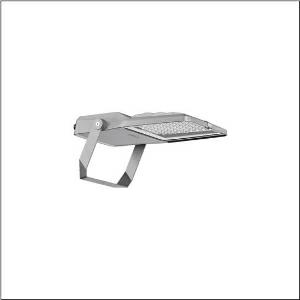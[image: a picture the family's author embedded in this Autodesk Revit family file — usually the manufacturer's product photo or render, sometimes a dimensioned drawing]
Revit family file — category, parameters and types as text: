
# Revit family: floodlight_fl_21_iq_mini___pl33t_5xa7771d2f1a_9c88
name_source: partatom
category: Lighting Fixtures
units: mm (PartAtom-declared; Revit-internal decimal feet)

## family parameters
Cut with Voids When Loaded = No
Host = Face
Light Source = No
Part Type = Normal
Room Calculation Point = No
Round Connector Dimension = Use Diameter
Shared = No

## types (1)
- --- (1 x LED, 17620 lm, 143 W, 3000K)
    Apparent Load = 143 VA
    CIE Flux Codes = 26 75 99 100 100
    Color Rendering = 70
    Color Temperature = 3000K
    Default Elevation = 1800 mm
    Description = Floodlight FL 21 iQ mini, floodlight, primary light control with lens, of PMMA, primary optical cover: protective disc, of toughened safety glass, transparent, light distribution: PL33T, light emission: direct distribution, installation type: surface-mounted, LED, High Power LED, rated luminous flux: 17.620lm, luminous efficacy: 123lm/W, light colour: 730, colour temperature: 3000K, control gear: iQ Comfort/DALI, control: Auto-Match, Temp-Guard, Lumen-Switch, Night-Set, Smart-Wire, Light-Fading, Desk-Remote (wireless, voltage-free reading and setting of iQ features in the workshop via application-optimized NFC function/RFID function), optimised constant luminous flux control (CLO 2.0), with terminal, 6-pole, mains connection: 220..240V, AC, 50/60Hz, start of lifetime: 143W, end of service life: 152W, reduction: 61W, luminaire housing, of diecast aluminium, powder-coated, Siteco® metallic grey (DB 702S), corrosivity category C5 mid according to DIN EN ISO 12944, suitable for swimming pools, chlorine-resistant, sealing non-destructively replaceable, mounting bracket, of steel, galvanised, powder-coated, Siteco® metallic grey (DB 702S), protection rating (complete): IP66, insulation class (complete): insulation class II (safety insulation), certification: CE, ENEC, VDE, protection symbol: D, impact resistance: IK08, permissible operating ambient temperature: -40..+40°C, permissible operating ambient temperature for outdoor applications: -40..+50°C, standard: DIN EN 12944, LABS conformity tested according to VDMA 24364:2018-05, packaging unit: 1 piece

Light Distribution: PL33T
    Height = 70 mm
    Lamp = 1 x LED
    Lamp Light Flux = 17620 lm
    Lamp Power = 143 W
    Lamp count = 1
    Length = 485 mm
    Luminous efficacy = 123 lm/W
    Manufacturer = Siteco
    ModVariant = No
    Model = 5XA7771D2F1A
    Number of Poles = 1
    OnlyDefault = Yes
    Power Factor = 1
    Product Name = Floodlight FL 21 iQ mini | PL33T
    Product group = floodlight | pylon annexe
    ProductGroupID = 6200
    Protection Class = Protection class II
    Protection Degree = IP 66
    RLX_Detail_Level = 1
    RLX_Emergency_Light_Flux = 0 lm
    RLX_Emergency_Type = 0
    RLX_Emergency_Type_DB = No
    RlxData = <blob elided: 96333 chars, md5=5826cdad>
    Socket = socket
    Standby Power = 0 W
    System Light Flux = 17620 lm
    System Power = 143 W
    Type Comments = factory setting: luminous flux: 100 % | dim-lin: 254 | 730 mA
    Type Image = l_1006845.jpg
    URL = http://relux.com
    VarID = @adj_149274
    Voltage = 0 V
    Weight = 0.00 kg
    Width = 337 mm

## geometry (parser evidence)
native form markers: Blend x4, Sweep x13
no freeform markers — native parametric forms only
